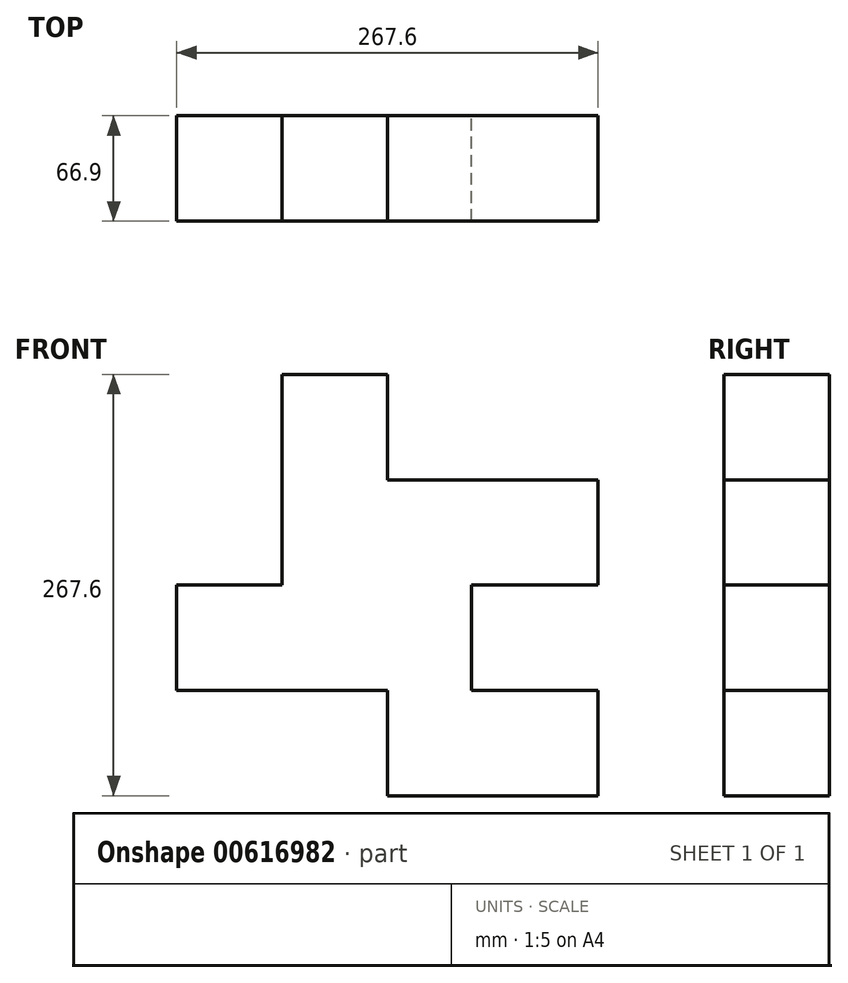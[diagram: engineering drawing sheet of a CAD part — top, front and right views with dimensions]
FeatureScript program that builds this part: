
annotation { "Feature Type Name" : "Feature", "Feature Type Description" : "" }
export const myFeature = defineFeature(function(context is Context, id is Id, definition is map)
    precondition{}
    {
        {
            var Q0;
            Q0=qCreatedBy(makeId("Front.planeOp"),FACE);
            var sketch = newSketch(context, id + "F0", { "sketchPlane" : qUnion([Q0])});
            skLineSegment(sketch, "E0", {"start": v(-151.25, 9.28) * mm, "end": v(-84.35, 9.28) * mm});
            skLineSegment(sketch, "E1", {"start": v(-84.35, 9.28) * mm, "end": v(-84.35, 143.08) * mm});
            skLineSegment(sketch, "E2", {"start": v(-84.35, 143.08) * mm, "end": v(-17.45, 143.08) * mm});
            skLineSegment(sketch, "E3", {"start": v(-17.45, 143.08) * mm, "end": v(-17.45, 76.18) * mm});
            skLineSegment(sketch, "E4", {"start": v(-17.45, 76.18) * mm, "end": v(116.35, 76.18) * mm});
            skLineSegment(sketch, "E5", {"start": v(116.35, 76.18) * mm, "end": v(116.35, 9.28) * mm});
            skLineSegment(sketch, "E6", {"start": v(116.35, 9.28) * mm, "end": v(36.07, 9.28) * mm});
            skLineSegment(sketch, "E7", {"start": v(36.07, 9.28) * mm, "end": v(36.07, -57.62) * mm});
            skLineSegment(sketch, "E8", {"start": v(36.07, -57.62) * mm, "end": v(116.35, -57.62) * mm});
            skLineSegment(sketch, "E9", {"start": v(116.35, -57.62) * mm, "end": v(116.35, -124.52) * mm});
            skLineSegment(sketch, "E10", {"start": v(116.35, -124.52) * mm, "end": v(-17.45, -124.52) * mm});
            skLineSegment(sketch, "E11", {"start": v(-17.45, -124.52) * mm, "end": v(-17.45, -57.62) * mm});
            skLineSegment(sketch, "E12", {"start": v(-17.45, -57.62) * mm, "end": v(-151.25, -57.62) * mm});
            skLineSegment(sketch, "E13", {"start": v(-151.25, -57.62) * mm, "end": v(-151.25, 9.28) * mm});
            skSolve(sketch);
        }
        {
            var Q0;
            Q0=makeQuery(id+"F0.imprint","IMPRINT",FACE,{"disambiguationData":[TD([[makeQuery(id+"F0.imprint","IMPRINT",EDGE,{"derivedFrom":sQuery(id+"F0.wireOp",EDGE,"E0")}),-1.0]])]});
            extrude(context, id + "F1", {"entities" : qUnion([Q0]), "depth" : 66.9 * mm, "offsetDistance" : 25 * mm});
        }
    });
